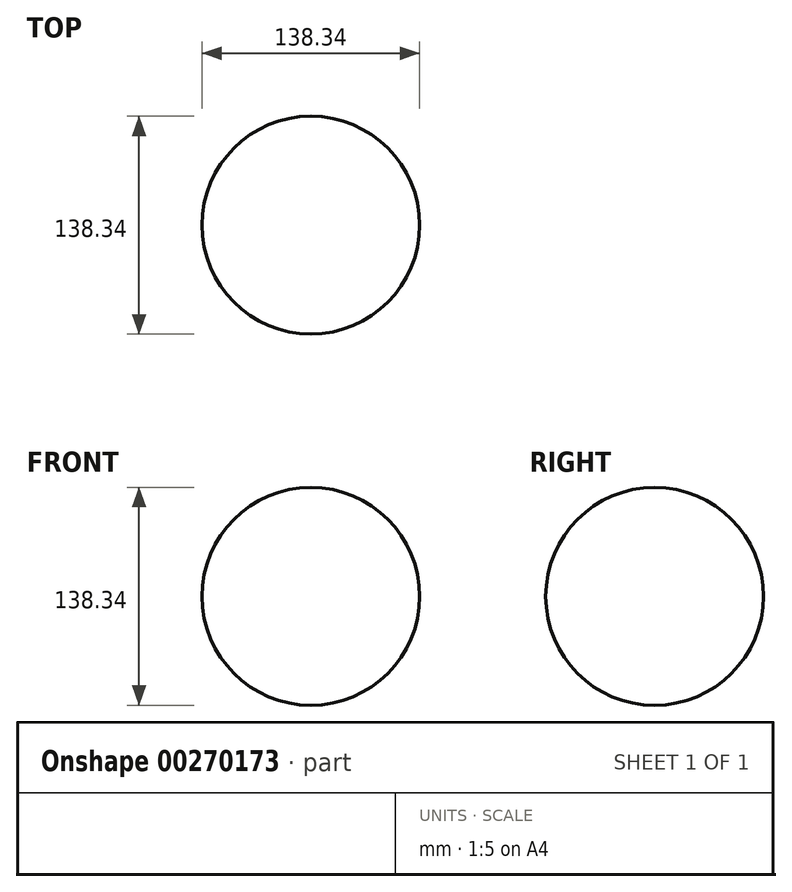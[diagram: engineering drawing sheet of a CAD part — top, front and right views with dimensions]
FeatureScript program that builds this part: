
annotation { "Feature Type Name" : "Feature", "Feature Type Description" : "" }
export const myFeature = defineFeature(function(context is Context, id is Id, definition is map)
    precondition{}
    {
        {
            var Q0;
            Q0=qCreatedBy(makeId("Front.planeOp"),FACE);
            var sketch = newSketch(context, id + "F0", { "sketchPlane" : qUnion([Q0])});
            skArc(sketch, "E0", {"start": v(0, 69.17) * mm, "mid": v(-69.17, 0) * mm, "end": v(0, -69.17) * mm});
            skLineSegment(sketch, "E1", {"start": v(0, 0) * mm, "end": v(0, 28.7) * mm, "construction": true});
            skLineSegment(sketch, "E2", {"start": v(0, 69.17) * mm, "end": v(0, -69.17) * mm});
            skSolve(sketch);
        }
        {
            var Q0;
            Q0=makeQuery(id+"F0.imprint","IMPRINT",FACE,{"disambiguationData":[TD([[makeQuery(id+"F0.imprint","IMPRINT",EDGE,{"derivedFrom":sQuery(id+"F0.wireOp",EDGE,"E0")}),1.0]])]});
            var Q1;
            Q1=sQuery(id+"F0.wireOp",EDGE,"E2");
            revolve(context, id + "F1", {"entities" : qUnion([Q0]), "axis" : qUnion([Q1]), "revolveType" : RevolveType.FULL});
        }
    });
